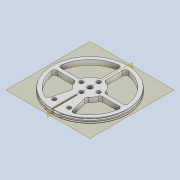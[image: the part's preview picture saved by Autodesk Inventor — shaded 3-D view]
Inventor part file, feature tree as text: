
AUTODESK INVENTOR PART (.ipt)
format: ipt  version: 2020 (Build 240168000, 168)  size: 300,032 bytes
history: native  units: mm
features: sketch x8, extrude x7, mirror x5, projected_geometry x4, plane x3, chamfer x2, revolve x1, fillet x1
ambient origin geometry x8: Origin, YZ Plane, XZ Plane, XY Plane, X Axis, Y Axis, Z Axis, Center Point
bodies: Solid1 (feature_tree)
feature tree (31):
  extrude  "Extrusion1"  Depth=2.0mm TaperAngle=0.0deg
  revolve  "Revolution1"  [1 undecoded]
  extrude  "Extrusion2"  Depth=3.0mm
  extrude  "Extrusion3"  Depth=2.0mm
  plane  "Work Plane1"
  extrude  "Extrusion4"  Depth=2.0mm TaperAngle=0.0deg
  mirror  "Mirror1"
  extrude  "Extrusion5"  Depth=1.0mm TaperAngle=0.0deg
  mirror  "Mirror2"
  plane  "Work Plane2"
  mirror  "Mirror3"
  chamfer  "Chamfer1"  Distance=3.2mm
  extrude  "Extrusion6"  Depth=2.0mm TaperAngle=0.0deg
  extrude  "Extrusion7"  TaperAngle=0.0deg  [1 undecoded]
  mirror  "Mirror4"
  fillet  "Fillet1"  Radius=0.5mm
  mirror  "Mirror5"
  chamfer  "Chamfer2"  Distance=7.0mm
  sketch  "Sketch1"  dims[d0=60.0mm d1=2.0mm d2=0.0mm]
  sketch  "Sketch2"  dims[d3=1.0mm d4=1.0mm]
  sketch  "Sketch3"  dims[d5=90.0deg d6=3.0mm]
  sketch  "Sketch4"  dims[d7=2.0mm d8=0.0mm d9=20.0mm]
  projected_geometry  "Projected Loop1"
  sketch  "Sketch5"  dims[d10=1.0mm d11=2.0mm d12=0.0mm]
  projected_geometry  "Projected Loop2"
  sketch  "Sketch6"  dims[d13=1.0mm d14=12.0mm d15=0.0mm]
  projected_geometry  "Projected Loop3"
  plane  "Work Plane3"
  sketch  "Sketch7"  dims[d16=6.0mm]
  sketch  "Sketch8"  dims[d17=23.0mm d18=3.2mm d19=12.0mm d20=0.0mm d21=0.0mm d22=0.5mm d23=2.0mm d24=45.0deg d25=7.0mm d26=3.2mm d27=40.0mm d29=360.0deg d31=12.0mm d32=0.0mm d33=20.0mm d34=55.0mm d35=3.0mm d36=1.5mm d37=1.5mm d38=1.5mm d39=12.0mm d40=0.0mm d41=2.0mm d42=0.5mm d43=2.0mm d44=45.0deg]
  projected_geometry  "Projected Loop4"
note: 2 required parameter values undecoded (feature->parameter linkage not recoverable at this tier; creation-order binding heuristic only, values carry confidence <= 0.55)